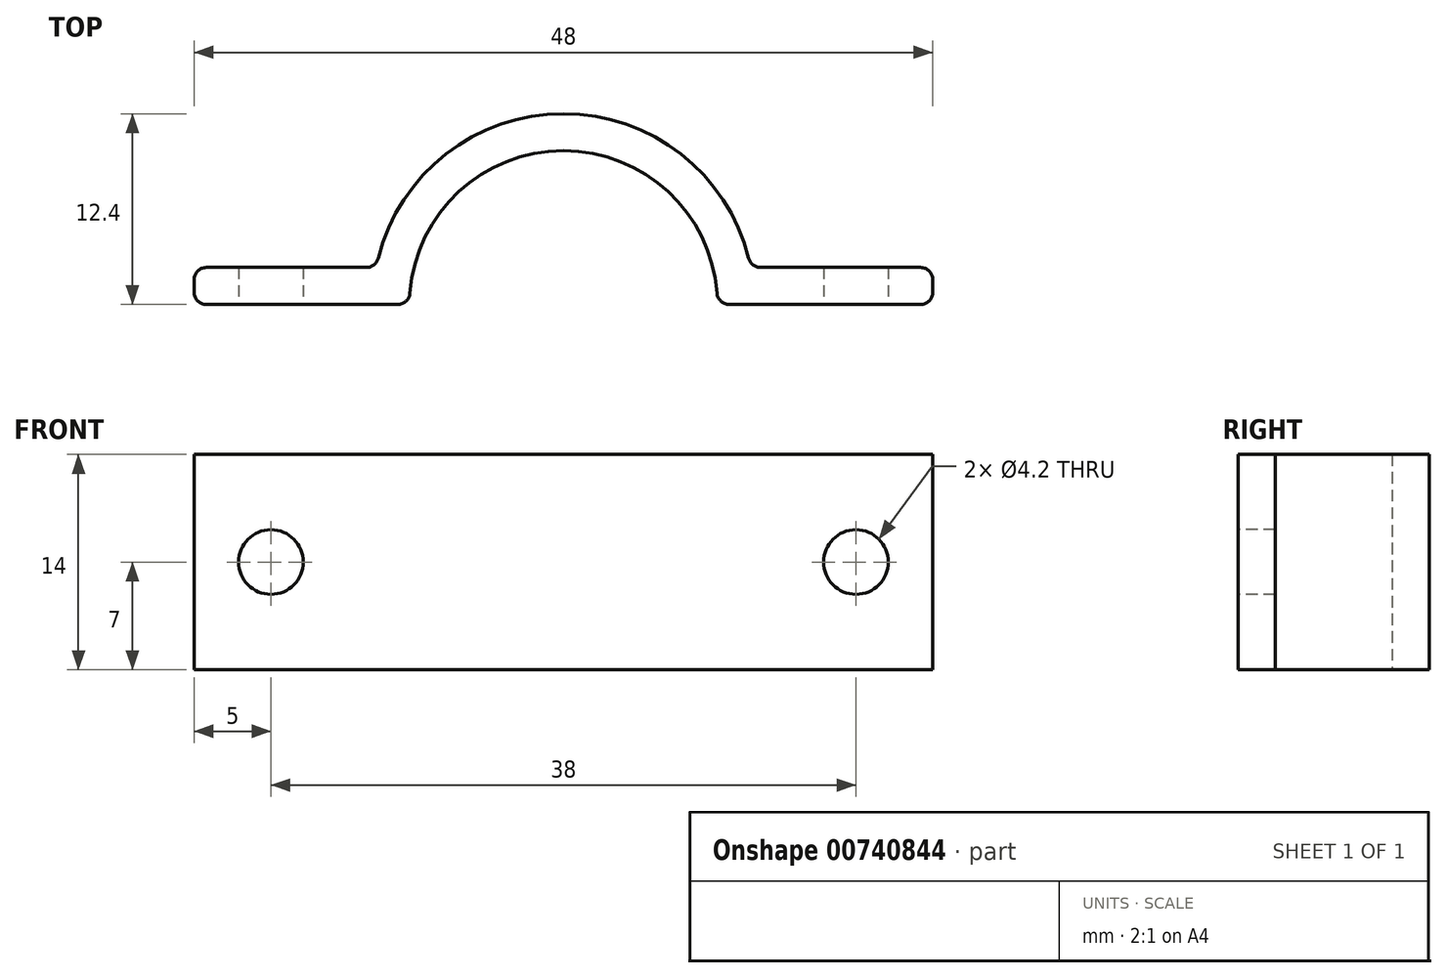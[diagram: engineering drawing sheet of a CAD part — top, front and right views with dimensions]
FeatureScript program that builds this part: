
annotation { "Feature Type Name" : "Feature", "Feature Type Description" : "" }
export const myFeature = defineFeature(function(context is Context, id is Id, definition is map)
    precondition{}
    {
        {
            var Q0;
            Q0=qCreatedBy(makeId("Top.planeOp"),FACE);
            var sketch = newSketch(context, id + "F0", { "sketchPlane" : qUnion([Q0])});
            skArc(sketch, "E0", {"start": v(9.97, 0.74) * mm, "mid": v(0, 10) * mm, "end": v(-9.97, 0.74) * mm});
            skLineSegment(sketch, "E1", {"start": v(0, 2.4) * mm, "end": v(0, 10) * mm, "construction": true});
            skArc(sketch, "E2.0", {"start": v(12.03, 3) * mm, "mid": v(0, 12.4) * mm, "end": v(-12.03, 3) * mm});
            skLineSegment(sketch, "E3.bottom", {"start": v(-23.2, 2.4) * mm, "end": v(-12.8, 2.4) * mm});
            skLineSegment(sketch, "E3.top", {"start": v(-23.2, 0) * mm, "end": v(-10.77, 0) * mm});
            skLineSegment(sketch, "E3.left", {"start": v(-24, 1.6) * mm, "end": v(-24, 0.8) * mm});
            skLineSegment(sketch, "E4.MirrorCS", {"start": v(23.2, 2.4) * mm, "end": v(12.8, 2.4) * mm});
            skLineSegment(sketch, "E5.MirrorCS", {"start": v(23.2, 0) * mm, "end": v(10.77, 0) * mm});
            skLineSegment(sketch, "E6.MirrorCS", {"start": v(24, 1.6) * mm, "end": v(24, 0.8) * mm});
            skPoint(sketch, "E7.orphan", {"position": v(0, 2.4) * mm});
            skPoint(sketch, "E8.visualSharp", {"position": v(-24, 2.4) * mm});
            skArc(sketch, "E8.filletArc", {"start": v(-23.2, 2.4) * mm, "mid": v(-23.77, 2.17) * mm, "end": v(-24, 1.6) * mm});
            skPoint(sketch, "E9.visualSharp", {"position": v(-24, 0) * mm});
            skArc(sketch, "E9.filletArc", {"start": v(-24, 0.8) * mm, "mid": v(-23.77, 0.23) * mm, "end": v(-23.2, 0) * mm});
            skPoint(sketch, "E10.visualSharp", {"position": v(-12.17, 2.4) * mm});
            skArc(sketch, "E10.filletArc", {"start": v(-12.8, 2.4) * mm, "mid": v(-12.31, 2.57) * mm, "end": v(-12.03, 3) * mm});
            skPoint(sketch, "E11.visualSharp", {"position": v(-10, 0) * mm});
            skArc(sketch, "E11.filletArc", {"start": v(-10.77, 0) * mm, "mid": v(-10.23, 0.21) * mm, "end": v(-9.97, 0.74) * mm});
            skPoint(sketch, "E12.visualSharp", {"position": v(12.17, 2.4) * mm});
            skArc(sketch, "E12.filletArc", {"start": v(12.03, 3) * mm, "mid": v(12.31, 2.57) * mm, "end": v(12.8, 2.4) * mm});
            skPoint(sketch, "E13.visualSharp", {"position": v(10, 0) * mm});
            skArc(sketch, "E13.filletArc", {"start": v(9.97, 0.74) * mm, "mid": v(10.23, 0.21) * mm, "end": v(10.77, 0) * mm});
            skPoint(sketch, "E14.visualSharp", {"position": v(24, 2.4) * mm});
            skArc(sketch, "E14.filletArc", {"start": v(24, 1.6) * mm, "mid": v(23.77, 2.17) * mm, "end": v(23.2, 2.4) * mm});
            skPoint(sketch, "E15.visualSharp", {"position": v(24, 0) * mm});
            skArc(sketch, "E15.filletArc", {"start": v(23.2, 0) * mm, "mid": v(23.77, 0.23) * mm, "end": v(24, 0.8) * mm});
            skSolve(sketch);
        }
        {
            var Q0;
            Q0 = qSketchRegion(id + "F0", true);
            extrude(context, id + "F1", {"entities" : qUnion([Q0]), "depth" : 14 * mm, "offsetDistance" : 25 * mm});
        }
        {
            var Q0;
            Q0=makeQuery(id+"F1.opExtrude","SWEPT_FACE",FACE,{"disambiguationData":[OSD([sQuery(id+"F0.wireOp",EDGE,"E3.top")])]});
            var sketch = newSketch(context, id + "F2", { "sketchPlane" : qUnion([Q0])});
            skPoint(sketch, "E16", {"position": v(-19, 0) * mm});
            skPoint(sketch, "E17", {"position": v(-23.2, 7) * mm});
            skPoint(sketch, "E18", {"position": v(23.2, 7) * mm});
            skPoint(sketch, "E19", {"position": v(16.99, 0) * mm});
            skCircle(sketch, "E20", {"center": v(19, 7) * mm, "radius": 2.1 * mm});
            skCircle(sketch, "E21", {"center": v(-19, 7) * mm, "radius": 2.1 * mm});
            skPoint(sketch, "E22.orphan", {"position": v(0, 7) * mm});
            skLineSegment(sketch, "E23", {"start": v(0, 7) * mm, "end": v(19, 7) * mm, "construction": true});
            skLineSegment(sketch, "E24", {"start": v(0, 7) * mm, "end": v(-19, 7) * mm, "construction": true});
            skSolve(sketch);
        }
        {
            var Q0;
            Q0 = qSketchRegion(id + "F2", true);
            extrude(context, id + "F3", {"entities" : qUnion([Q0]), "operationType" : NewBodyOperationType.REMOVE, "endBound" : BoundingType.THROUGH_ALL, "oppositeDirection" : true, "depth" : 25 * mm, "offsetDistance" : 25 * mm});
        }
    });
